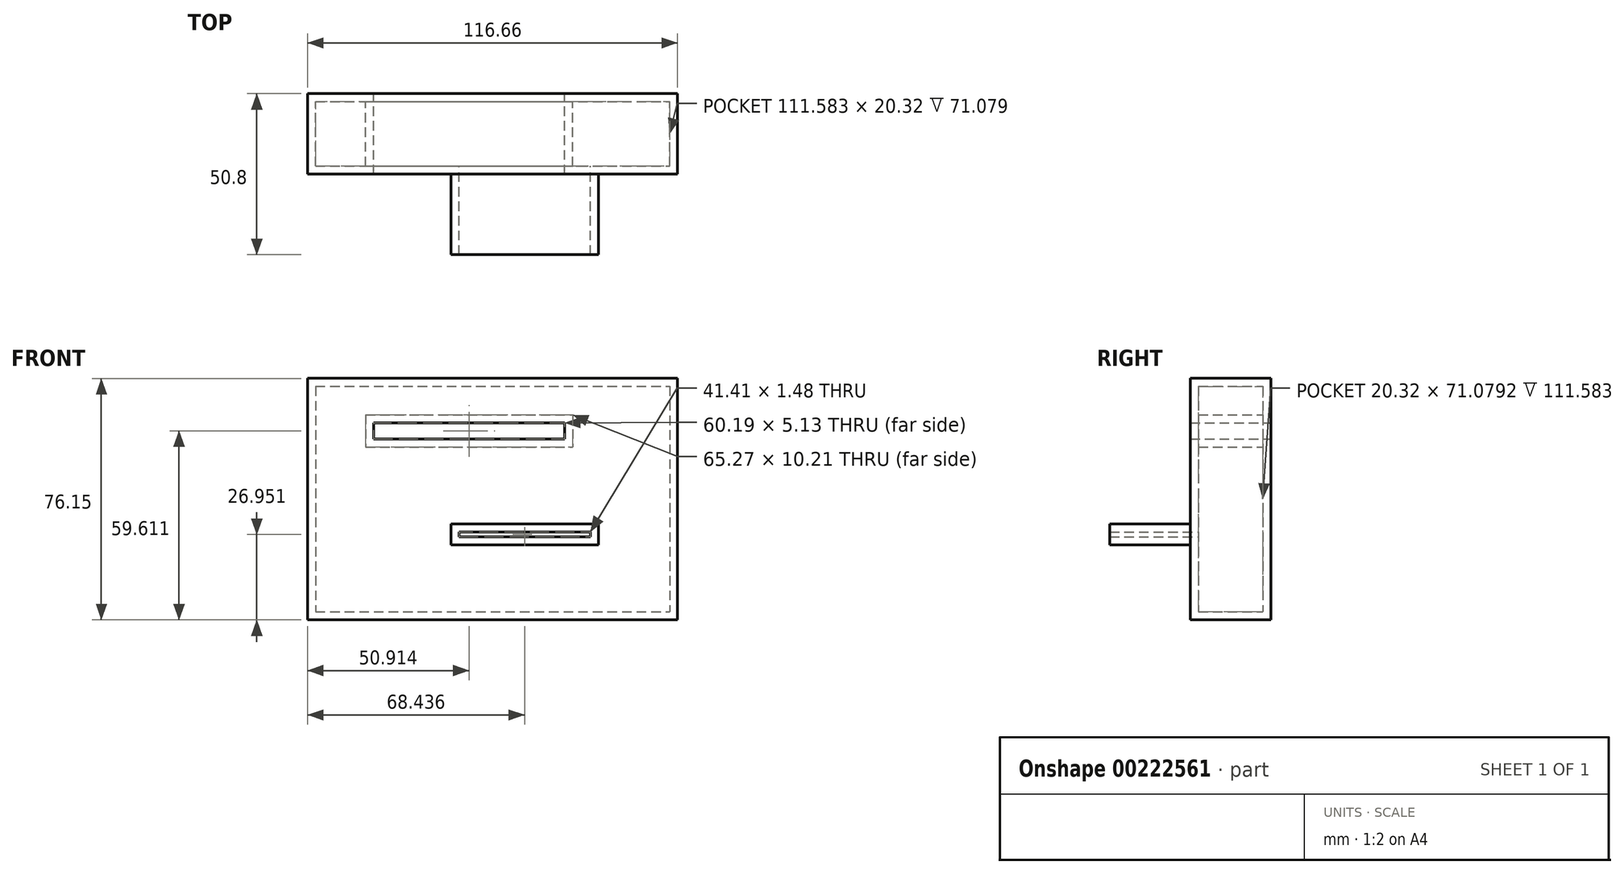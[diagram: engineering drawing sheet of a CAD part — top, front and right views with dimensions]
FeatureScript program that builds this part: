
annotation { "Feature Type Name" : "Feature", "Feature Type Description" : "" }
export const myFeature = defineFeature(function(context is Context, id is Id, definition is map)
    precondition{}
    {
        {
            var Q0;
            Q0=qCreatedBy(makeId("Front.planeOp"),FACE);
            var sketch = newSketch(context, id + "F0", { "sketchPlane" : qUnion([Q0])});
            skLineSegment(sketch, "E0.bottom", {"start": v(-31.1, 32.37) * mm, "end": v(85.57, 32.37) * mm});
            skLineSegment(sketch, "E0.top", {"start": v(-31.1, -43.78) * mm, "end": v(85.57, -43.78) * mm});
            skLineSegment(sketch, "E0.left", {"start": v(-31.1, 32.37) * mm, "end": v(-31.1, -43.78) * mm});
            skLineSegment(sketch, "E0.right", {"start": v(85.57, 32.37) * mm, "end": v(85.57, -43.78) * mm});
            skLineSegment(sketch, "E1.bottom", {"start": v(-10.27, 18.4) * mm, "end": v(49.92, 18.4) * mm});
            skLineSegment(sketch, "E1.top", {"start": v(-10.27, 13.26) * mm, "end": v(49.92, 13.26) * mm});
            skLineSegment(sketch, "E1.left", {"start": v(-10.27, 18.4) * mm, "end": v(-10.27, 13.26) * mm});
            skLineSegment(sketch, "E1.right", {"start": v(49.92, 18.4) * mm, "end": v(49.92, 13.26) * mm});
            skSolve(sketch);
        }
        {
            var Q0;
            Q0=makeQuery(id+"F0.imprint","IMPRINT",FACE,{"disambiguationData":[TD([[makeQuery(id+"F0.imprint","IMPRINT",EDGE,{"derivedFrom":sQuery(id+"F0.wireOp",EDGE,"E0.bottom")}),-1.0]])]});
            extrude(context, id + "F1", {"entities" : qUnion([Q0]), "depth" : 25.4 * mm});
        }
        {
            var Q0;
            Q0=makeQuery(id+"F1.opExtrude","CAP_FACE",FACE,{"disambiguationData":[OSD([sQuery(id+"F0.wireOp",EDGE,"E0.bottom"),sQuery(id+"F0.wireOp",EDGE,"E0.top"),sQuery(id+"F0.wireOp",EDGE,"E0.left"),sQuery(id+"F0.wireOp",EDGE,"E0.right"),sQuery(id+"F0.wireOp",EDGE,"E1.bottom"),sQuery(id+"F0.wireOp",EDGE,"E1.top"),sQuery(id+"F0.wireOp",EDGE,"E1.left"),sQuery(id+"F0.wireOp",EDGE,"E1.right")])],"isStart":false});
            var sketch = newSketch(context, id + "F2", { "sketchPlane" : qUnion([Q0])});
            skLineSegment(sketch, "E2.bottom", {"start": v(14.1, -13.55) * mm, "end": v(60.6, -13.55) * mm});
            skLineSegment(sketch, "E2.top", {"start": v(14.1, -20.1) * mm, "end": v(60.6, -20.1) * mm});
            skLineSegment(sketch, "E2.left", {"start": v(14.1, -13.55) * mm, "end": v(14.1, -20.1) * mm});
            skLineSegment(sketch, "E2.right", {"start": v(60.6, -13.55) * mm, "end": v(60.6, -20.1) * mm});
            skSolve(sketch);
        }
        {
            var Q0;
            Q0=makeQuery(id+"F2.imprint","IMPRINT",FACE,{"disambiguationData":[TD([[makeQuery(id+"F2.imprint","IMPRINT",EDGE,{"derivedFrom":sQuery(id+"F2.wireOp",EDGE,"E2.bottom")}),-1.0]])]});
            extrude(context, id + "F3", {"entities" : qUnion([Q0]), "operationType" : NewBodyOperationType.ADD, "depth" : 25.4 * mm});
        }
        {
            var Q0;
            Q0=makeQuery(id+"F3.opExtrude","CAP_FACE",FACE,{"disambiguationData":[OSD([sQuery(id+"F2.wireOp",EDGE,"E2.bottom"),sQuery(id+"F2.wireOp",EDGE,"E2.top"),sQuery(id+"F2.wireOp",EDGE,"E2.left"),sQuery(id+"F2.wireOp",EDGE,"E2.right")])],"isStart":false});
            shell(context, id + "F4", {"entities" : qUnion([Q0]), "thickness" : 2.54 * mm});
        }
    });
